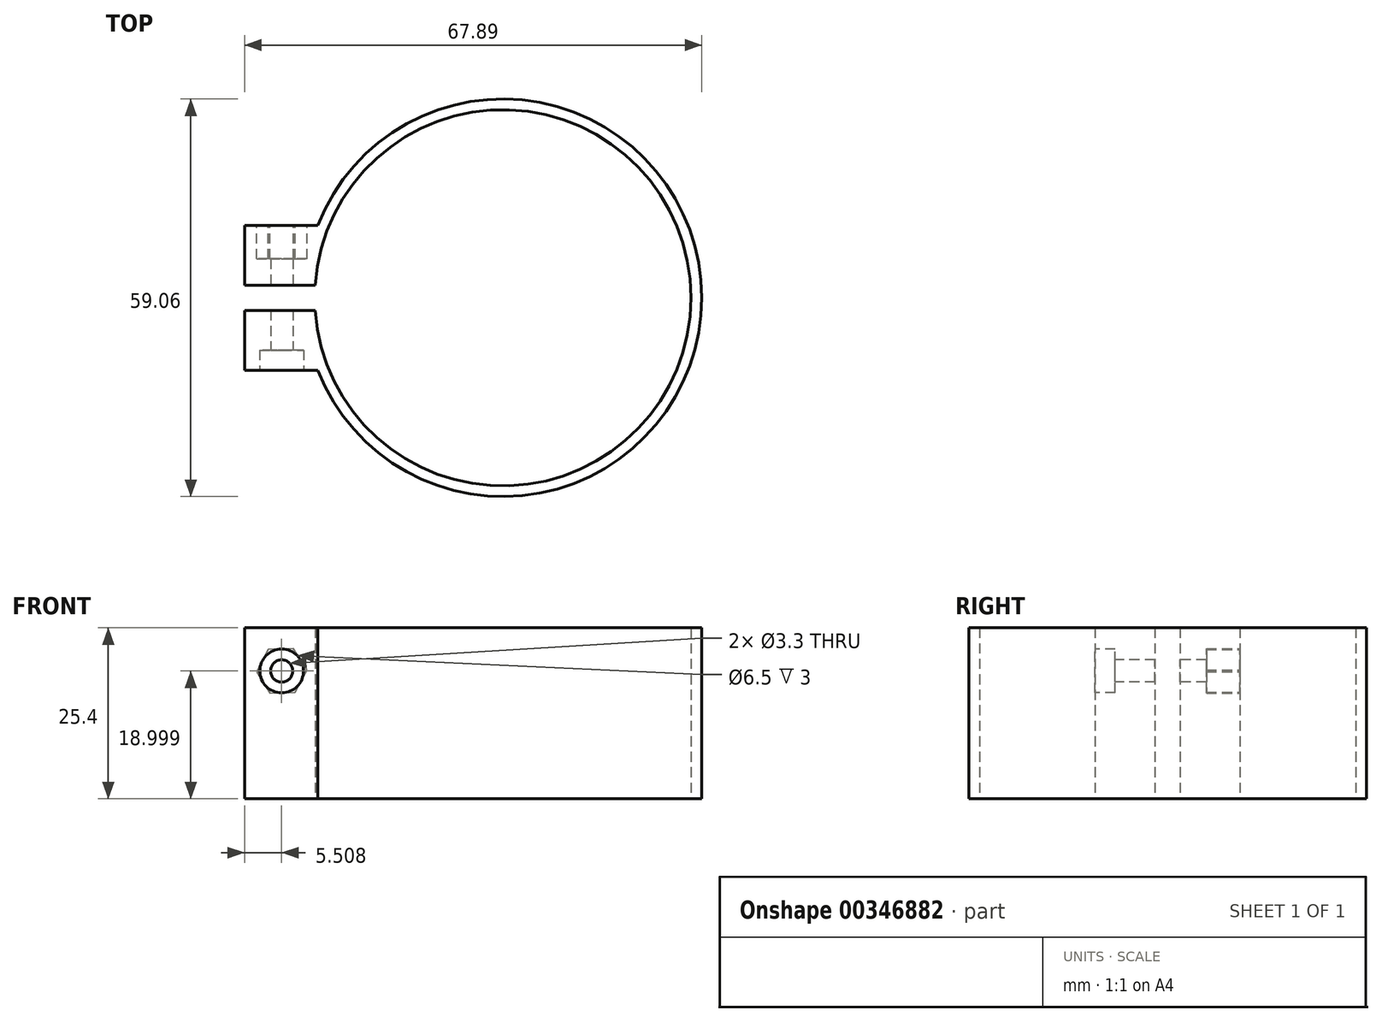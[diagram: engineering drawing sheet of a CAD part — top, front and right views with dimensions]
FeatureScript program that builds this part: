
annotation { "Feature Type Name" : "Feature", "Feature Type Description" : "" }
export const myFeature = defineFeature(function(context is Context, id is Id, definition is map)
    precondition{}
    {
        {
            var Q0;
            Q0=qCreatedBy(makeId("Top.planeOp"),FACE);
            var sketch = newSketch(context, id + "F0", { "sketchPlane" : qUnion([Q0])});
            skArc(sketch, "E0", {"start": v(-27.88, -1.88) * mm, "mid": v(27.94, 0) * mm, "end": v(-27.88, 1.88) * mm});
            skArc(sketch, "E1.0", {"start": v(-27.5, -10.77) * mm, "mid": v(29.53, 0) * mm, "end": v(-27.5, 10.77) * mm});
            skLineSegment(sketch, "E2.bottom", {"start": v(-27.88, -1.88) * mm, "end": v(-29.47, -1.88) * mm});
            skLineSegment(sketch, "E2.top", {"start": v(-27.88, 1.88) * mm, "end": v(-29.47, 1.88) * mm});
            skLineSegment(sketch, "E3.bottom", {"start": v(-29.47, 1.88) * mm, "end": v(-38.36, 1.88) * mm});
            skLineSegment(sketch, "E3.top", {"start": v(-29.47, 10.77) * mm, "end": v(-38.36, 10.77) * mm});
            skLineSegment(sketch, "E3.right", {"start": v(-38.36, 1.88) * mm, "end": v(-38.36, 10.77) * mm});
            skLineSegment(sketch, "E4.bottom", {"start": v(-29.47, -1.88) * mm, "end": v(-38.36, -1.88) * mm});
            skLineSegment(sketch, "E4.top", {"start": v(-29.47, -10.77) * mm, "end": v(-38.36, -10.77) * mm});
            skLineSegment(sketch, "E4.right", {"start": v(-38.36, -1.88) * mm, "end": v(-38.36, -10.77) * mm});
            skLineSegment(sketch, "E5", {"start": v(-29.47, 10.77) * mm, "end": v(-27.5, 10.77) * mm});
            skLineSegment(sketch, "E6", {"start": v(-29.47, -10.77) * mm, "end": v(-27.5, -10.77) * mm});
            skSolve(sketch);
        }
        {
            var Q0;
            Q0=makeQuery(id+"F0.imprint","IMPRINT",FACE,{"disambiguationData":[TD([[makeQuery(id+"F0.imprint","IMPRINT",EDGE,{"derivedFrom":sQuery(id+"F0.wireOp",EDGE,"E0")}),-1.0]])]});
            extrude(context, id + "F1", {"entities" : qUnion([Q0]), "depth" : 25.4 * mm});
        }
        {
            var Q0;
            Q0=makeQuery(id+"F1.opExtrude","SWEPT_FACE",FACE,{"disambiguationData":[OSD([sQuery(id+"F0.wireOp",EDGE,"E4.top"),sQuery(id+"F0.wireOp",EDGE,"E6")])]});
            var sketch = newSketch(context, id + "F2", { "sketchPlane" : qUnion([Q0])});
            skLineSegment(sketch, "E7", {"start": v(-32.93, 25.4) * mm, "end": v(-32.93, 0) * mm});
            skPoint(sketch, "E8", {"position": v(-32.85, 19) * mm});
            skSolve(sketch);
        }
        {
            var Q0;
            Q0=sQuery(id+"F2.wireOp",VERTEX,"E8");
            var Q1;
            Q1=makeQuery(id+"F1.opExtrude","SWEPT_BODY",BODY,{"disambiguationData":[OSD([sQuery(id+"F0.wireOp",EDGE,"E0"),sQuery(id+"F0.wireOp",EDGE,"E1.0"),sQuery(id+"F0.wireOp",EDGE,"E2.bottom"),sQuery(id+"F0.wireOp",EDGE,"E2.top"),sQuery(id+"F0.wireOp",EDGE,"E3.bottom"),sQuery(id+"F0.wireOp",EDGE,"E3.top"),sQuery(id+"F0.wireOp",EDGE,"E3.right"),sQuery(id+"F0.wireOp",EDGE,"E4.bottom"),sQuery(id+"F0.wireOp",EDGE,"E4.top"),sQuery(id+"F0.wireOp",EDGE,"E4.right"),sQuery(id+"F0.wireOp",EDGE,"E5"),sQuery(id+"F0.wireOp",EDGE,"E6")])]});
            hole(context, id + "F3", {"style" : HoleStyle.C_BORE, "endStyle" : HoleEndStyle.THROUGH, "standardTappedOrClearance" : lookupTablePath({ "standard" : "ISO", "fit" : "Normal", "size" : "M3", "type" : "Clearance" }), "standardBlindInLast" : lookupTablePath({ "fit" : "Standard", "standard" : "ISO", "size" : "M3", "type" : "Clearance" }), "holeDiameter" : 3.3 * mm, "cBoreDiameter" : 6.5 * mm, "cBoreDepth" : 3 * mm, "locations" : qUnion([Q0]), "scope" : qUnion([Q1]), "isTappedThrough" : true});
        }
        {
            var Q0;
            Q0=makeQuery(id+"F1.opExtrude","SWEPT_FACE",FACE,{"disambiguationData":[OSD([sQuery(id+"F0.wireOp",EDGE,"E3.top"),sQuery(id+"F0.wireOp",EDGE,"E5")])]});
            var sketch = newSketch(context, id + "F4", { "sketchPlane" : qUnion([Q0])});
            skCircle(sketch, "E9.cCircle", {"center": v(32.85, 19) * mm, "radius": 3.25 * mm, "construction": true});
            skLineSegment(sketch, "E9.0", {"start": v(36.6, 18.86) * mm, "end": v(34.6, 15.69) * mm});
            skLineSegment(sketch, "E9.1", {"start": v(34.6, 15.69) * mm, "end": v(30.86, 15.82) * mm});
            skLineSegment(sketch, "E9.2", {"start": v(30.86, 15.82) * mm, "end": v(29.1, 19.13) * mm});
            skLineSegment(sketch, "E9.3", {"start": v(29.1, 19.13) * mm, "end": v(31.1, 22.31) * mm});
            skLineSegment(sketch, "E9.4", {"start": v(31.1, 22.31) * mm, "end": v(34.84, 22.18) * mm});
            skLineSegment(sketch, "E9.5", {"start": v(34.84, 22.18) * mm, "end": v(36.6, 18.86) * mm});
            skPoint(sketch, "E9.0.midPoint", {"position": v(35.6, 17.27) * mm});
            skSolve(sketch);
        }
        {
            var Q0;
            Q0=qSketchRegion(id+"F4",true);
            extrude(context, id + "F5", {"entities" : qUnion([Q0]), "operationType" : NewBodyOperationType.REMOVE, "oppositeDirection" : true, "depth" : 5 * mm});
        }
    });
